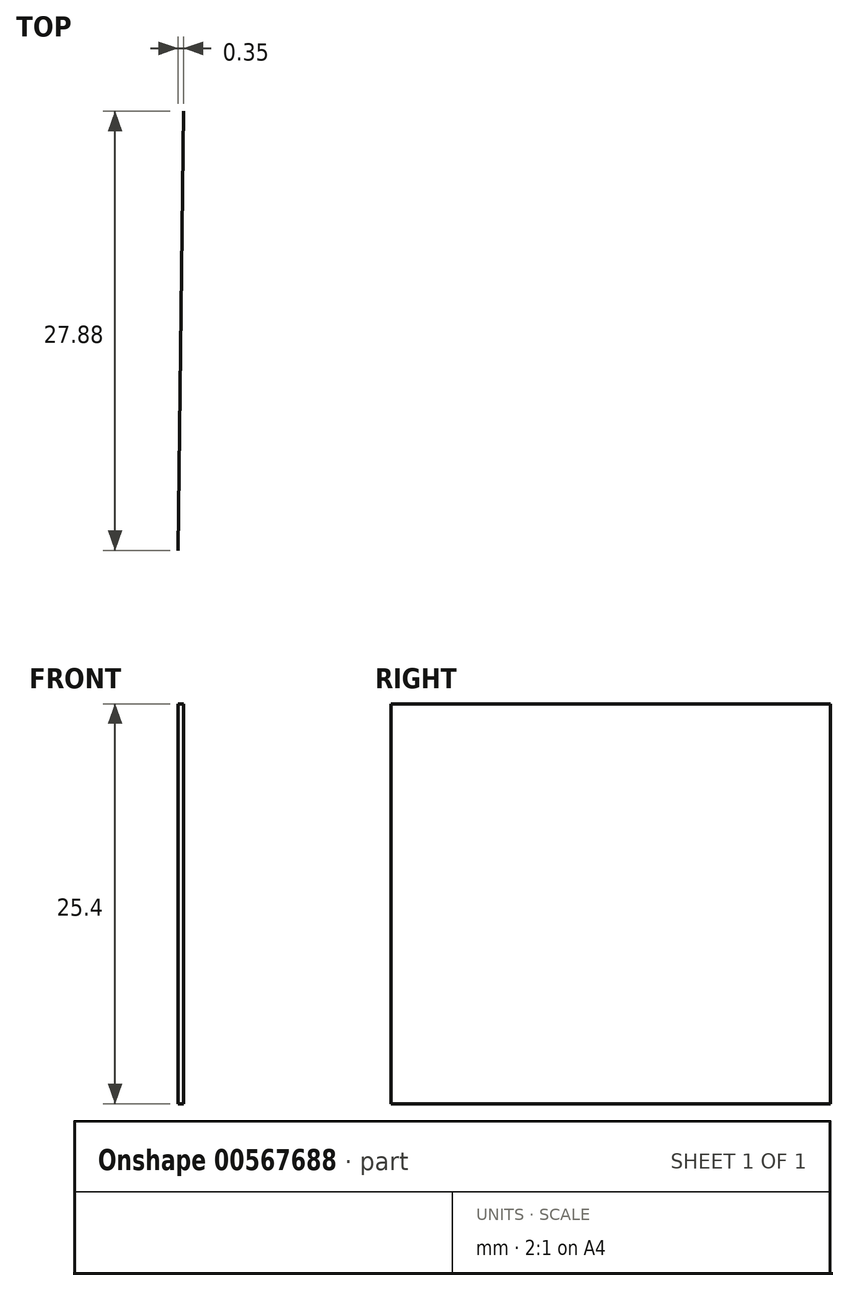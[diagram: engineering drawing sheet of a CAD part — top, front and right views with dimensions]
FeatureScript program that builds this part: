
annotation { "Feature Type Name" : "Feature", "Feature Type Description" : "" }
export const myFeature = defineFeature(function(context is Context, id is Id, definition is map)
    precondition{}
    {
        {
            var Q0;
            Q0=qCreatedBy(makeId("Top.planeOp"),FACE);
            var sketch = newSketch(context, id + "F0", { "sketchPlane" : qUnion([Q0])});
            skLineSegment(sketch, "E0", {"start": v(-31.06, -35.06) * mm, "end": v(44, -35.06) * mm});
            skLineSegment(sketch, "E1", {"start": v(44, 30.01) * mm, "end": v(44, -35.06) * mm});
            skLineSegment(sketch, "E2", {"start": v(17.14, 17.96) * mm, "end": v(44, 30.01) * mm});
            skLineSegment(sketch, "E3", {"start": v(16.8, -9.92) * mm, "end": v(17.14, 17.96) * mm});
            skLineSegment(sketch, "E4", {"start": v(-19.7, -5.8) * mm, "end": v(-31.06, -35.06) * mm});
            skArc(sketch, "E5", {"start": v(0, -5.8) * mm, "mid": v(-9.85, 5.7) * mm, "end": v(-19.7, -5.8) * mm});
            skSolve(sketch);
        }
        {
            var Q0;
            Q0=sQuery(id+"F0.wireOp",EDGE,"E3");
            extrude(context, id + "F1", {"bodyType" : ToolBodyType.SURFACE, "surfaceEntities" : qUnion([Q0]), "depth" : 25.4 * mm, "offsetDistance" : 25.4 * mm});
        }
    });
